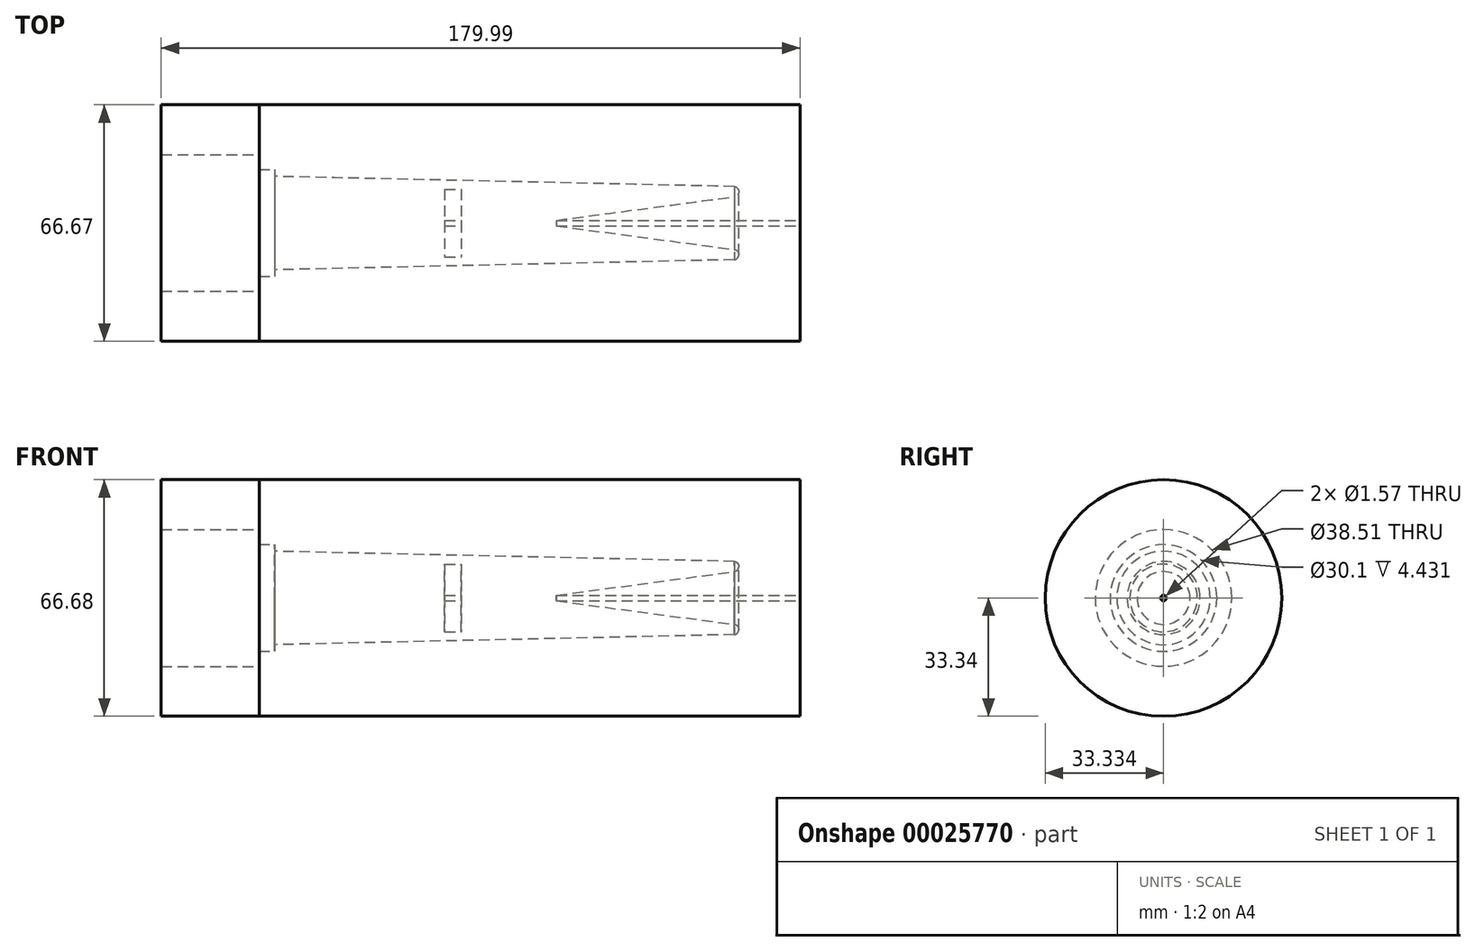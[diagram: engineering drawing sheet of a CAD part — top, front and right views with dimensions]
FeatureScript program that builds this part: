
annotation { "Feature Type Name" : "Feature", "Feature Type Description" : "" }
export const myFeature = defineFeature(function(context is Context, id is Id, definition is map)
    precondition{}
    {
        {
            var Q0;
            Q0=qCreatedBy(makeId("Top.planeOp"),FACE);
            var sketch = newSketch(context, id + "F0", { "sketchPlane" : qUnion([Q0])});
            skPoint(sketch, "E0", {"position": v(-79.97, 10.9) * mm});
            skPoint(sketch, "E1", {"position": v(-79.97, -55.78) * mm});
            skLineSegment(sketch, "E2", {"start": v(-79.97, 10.9) * mm, "end": v(-79.97, -55.78) * mm, "construction": true});
            skLineSegment(sketch, "E3", {"start": v(27.79, -22.45) * mm, "end": v(-112.43, -22.45) * mm, "construction": true});
            skPoint(sketch, "E3.startSnap0", {"position": v(-79.97, -22.45) * mm});
            skPoint(sketch, "E4", {"position": v(33.02, -23.4) * mm});
            skPoint(sketch, "E5", {"position": v(-27.7, -31.97) * mm});
            skPoint(sketch, "E6", {"position": v(-23, -31.97) * mm});
            skLineSegment(sketch, "E7", {"start": v(-27.7, -31.97) * mm, "end": v(-27.7, -23.23) * mm});
            skLineSegment(sketch, "E8", {"start": v(-27.7, -23.23) * mm, "end": v(-23, -23.23) * mm});
            skLineSegment(sketch, "E9", {"start": v(-23, -23.23) * mm, "end": v(-23, -31.97) * mm});
            skLineSegment(sketch, "E10", {"start": v(-27.7, -31.97) * mm, "end": v(-23, -31.97) * mm});
            skLineSegment(sketch, "E11", {"start": v(-79.97, -55.78) * mm, "end": v(72.43, -55.78) * mm});
            skLineSegment(sketch, "E12", {"start": v(72.43, -55.78) * mm, "end": v(72.43, 10.9) * mm});
            skLineSegment(sketch, "E13", {"start": v(72.43, 10.9) * mm, "end": v(-79.97, 10.9) * mm});
            skLineSegment(sketch, "E14", {"start": v(-79.97, -55.78) * mm, "end": v(-107.56, -55.78) * mm});
            skLineSegment(sketch, "E15", {"start": v(-107.56, -55.78) * mm, "end": v(-107.56, -41.7) * mm});
            skLineSegment(sketch, "E16", {"start": v(-107.56, -41.7) * mm, "end": v(-79.97, -41.7) * mm});
            skLineSegment(sketch, "E17", {"start": v(-79.97, -41.7) * mm, "end": v(-79.97, -55.78) * mm});
            skLineSegment(sketch, "E18", {"start": v(-79.97, -41.7) * mm, "end": v(-79.97, -37.5) * mm});
            skLineSegment(sketch, "E19", {"start": v(-79.97, -37.5) * mm, "end": v(-75.54, -37.5) * mm});
            skLineSegment(sketch, "E20", {"start": v(-75.54, -37.5) * mm, "end": v(-75.54, -35.61) * mm});
            skFitSpline(sketch, "E21", {"points": [v(-107.56, -44.6) * mm, v(-209.85, -45.95) * mm], "startDerivative": vector(-16.93, 87.6) * mm, "endDerivative": vector(-159.38, -19.95) * mm});
            skLineSegment(sketch, "E22", {"start": v(-209.85, -45.95) * mm, "end": v(-107.56, -44.6) * mm});
            skLineSegment(sketch, "E23", {"start": v(-75.54, -35.61) * mm, "end": v(72.43, -32.35) * mm});
            skLineSegment(sketch, "E24", {"start": v(3.81, -23.23) * mm, "end": v(72.43, -32.35) * mm});
            skLineSegment(sketch, "E25", {"start": v(3.81, -23.23) * mm, "end": v(64.23, -23.23) * mm});
            skLineSegment(sketch, "E26", {"start": v(64.23, -23.23) * mm, "end": v(72.43, -23.23) * mm});
            skArc(sketch, "E27", {"start": v(53.94, -32.75) * mm, "mid": v(55.19, -31.3) * mm, "end": v(53.88, -29.88) * mm});
            skSolve(sketch);
        }
        {
            var Q0;
            {var subQ1=sQuery(id+"F0.wireOp",EDGE,"E11");Q0=makeQuery(id+"F0.imprint","IMPRINT",FACE,{"disambiguationData":[TD([[makeQuery(id+"F0.imprint","IMPRINT",EDGE,{"derivedFrom":subQ1}),1.0]])]});}
            var Q1;
            {var subQ3=sQuery(id+"F0.wireOp",EDGE,"T56PlAEB-rPdA-lWn9-jRqS-IdodrreqzClt");Q1=makeQuery(id+"F0.imprint","IMPRINT",FACE,{"disambiguationData":[TD([[makeQuery(id+"F0.imprint","IMPRINT",EDGE,{"derivedFrom":subQ3}),-1.0]])]});}
            var Q2;
            {var subQ0=sQuery(id+"F0.wireOp",EDGE,"E25");Q2=makeQuery(id+"F0.imprint","IMPRINT",FACE,{"disambiguationData":[TD([[makeQuery(id+"F0.imprint","IMPRINT",EDGE,{"derivedFrom":subQ0}),-1.0]])]});}
            var Q3;
            {var subQ1=sQuery(id+"F0.wireOp",EDGE,"E23");var subQ3=sQuery(id+"F0.wireOp",EDGE,"E27");var subQ4=makeQuery(id+"F0.imprint","INTERSECT",VERTEX,{"derivedFrom":[subQ1,subQ3]});Q3=makeQuery(id+"F0.imprint","IMPRINT",FACE,{"disambiguationData":[TD([[makeQuery(id+"F0.imprint","IMPRINT",EDGE,{"disambiguationData":[TD([[subQ4,-1.0]])],"derivedFrom":subQ3}),-1.0]])]});}
            var Q4;
            Q4=sQuery(id+"F0.wireOp",EDGE,"E3");
            revolve(context, id + "F1", {"surfaceOperationType" : NewSurfaceOperationType.NEW, "entities" : qUnion([Q0, Q1, Q2, Q3]), "axis" : qUnion([Q4]), "revolveType" : RevolveType.FULL});
        }
        {
            var Q0;
            Q0=makeQuery(id+"F0.imprint","IMPRINT",FACE,{"disambiguationData":[TD([[makeQuery(id+"F0.imprint","IMPRINT",EDGE,{"derivedFrom":sQuery(id+"F0.wireOp",EDGE,"E14")}),-1.0]])]});
            var Q1;
            Q1=sQuery(id+"F0.wireOp",EDGE,"E3");
            revolve(context, id + "F2", {"surfaceOperationType" : NewSurfaceOperationType.NEW, "entities" : qUnion([Q0]), "axis" : qUnion([Q1]), "revolveType" : RevolveType.FULL});
        }
        {
            var Q0;
            Q0=makeQuery(id+"F0.imprint","IMPRINT",FACE,{"disambiguationData":[TD([[makeQuery(id+"F0.imprint","IMPRINT",EDGE,{"derivedFrom":sQuery(id+"F0.wireOp",EDGE,"E7")}),-1.0]])]});
            var Q1;
            Q1=sQuery(id+"F0.wireOp",EDGE,"E3");
            revolve(context, id + "F3", {"surfaceOperationType" : NewSurfaceOperationType.NEW, "entities" : qUnion([Q0]), "axis" : qUnion([Q1]), "revolveType" : RevolveType.FULL});
        }
        {
            var Q0;
            Q0=makeQuery(id+"F0.imprint","IMPRINT",FACE,{"disambiguationData":[TD([[makeQuery(id+"F0.imprint","IMPRINT",EDGE,{"derivedFrom":sQuery(id+"F0.wireOp",EDGE,"E21")}),1.0]])]});
            var Q1;
            Q1=sQuery(id+"F0.wireOp",EDGE,"E3");
            revolve(context, id + "F4", {"surfaceOperationType" : NewSurfaceOperationType.NEW, "entities" : qUnion([Q0]), "axis" : qUnion([Q1]), "revolveType" : RevolveType.FULL});
        }
        {
            var Q0;
            Q0=makeQuery(id+"F4.opRevolve","SWEPT_BODY",BODY,{"disambiguationData":[OSD([sQuery(id+"F0.wireOp",EDGE,"E21"),sQuery(id+"F0.wireOp",EDGE,"E22")])]});
            deleteBodies(context, id + "F5", {"entities" : qUnion([Q0])});
        }
    });
